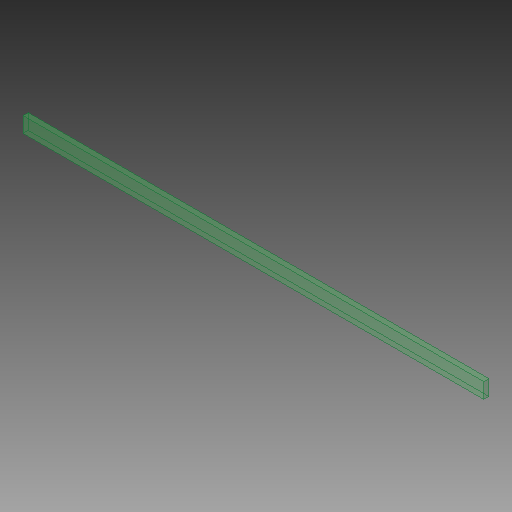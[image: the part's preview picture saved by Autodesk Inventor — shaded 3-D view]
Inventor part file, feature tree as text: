
AUTODESK INVENTOR PART (.ipt)
format: ipt  version: 2018.1 (Build 221171000, 171)  size: 89,088 bytes
history: native  units: mm
features: extrude x1, sketch x1
ambient origin geometry x8: Origin, YZ Plane, XZ Plane, XY Plane, X Axis, Y Axis, Z Axis, Center Point
bodies: Body1 (feature_tree)
feature tree (2):
  extrude  "Extrusion2"  Depth=15.0mm
  sketch  "Sketch2"  dims[d4=449.0mm d5=15.0mm d6=5.0mm d7=0.0mm]
